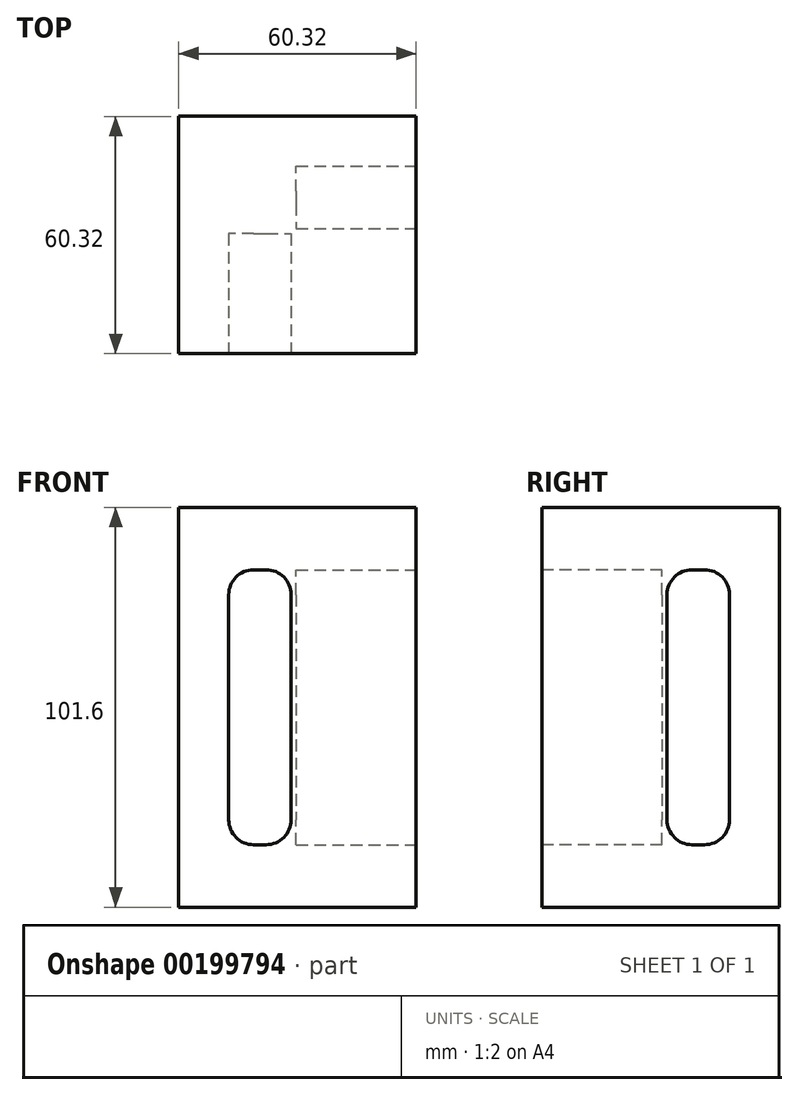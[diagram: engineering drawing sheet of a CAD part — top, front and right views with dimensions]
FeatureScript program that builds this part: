
annotation { "Feature Type Name" : "Feature", "Feature Type Description" : "" }
export const myFeature = defineFeature(function(context is Context, id is Id, definition is map)
    precondition{}
    {
        {
            var Q0;
            Q0=qCreatedBy(makeId("Top.planeOp"),FACE);
            var sketch = newSketch(context, id + "F0", { "sketchPlane" : qUnion([Q0])});
            skLineSegment(sketch, "E0.bottom", {"start": v(30.16, -30.16) * mm, "end": v(-30.16, -30.16) * mm});
            skLineSegment(sketch, "E0.top", {"start": v(30.16, 30.16) * mm, "end": v(-30.16, 30.16) * mm});
            skLineSegment(sketch, "E0.left", {"start": v(30.16, -30.16) * mm, "end": v(30.16, 30.16) * mm});
            skLineSegment(sketch, "E0.right", {"start": v(-30.16, -30.16) * mm, "end": v(-30.16, 30.16) * mm});
            skPoint(sketch, "E0.middle", {"position": v(0, 0) * mm});
            skSolve(sketch);
        }
        {
            var Q0;
            Q0 = qSketchRegion(id + "F0", true);
            extrude(context, id + "F1", {"entities" : qUnion([Q0]), "depth" : 101.6 * mm});
        }
        {
            var Q0;
            Q0=makeQuery(id+"F1.opExtrude","CAP_FACE",FACE,{"disambiguationData":[OSD([sQuery(id+"F0.wireOp",EDGE,"E0.bottom"),sQuery(id+"F0.wireOp",EDGE,"E0.top"),sQuery(id+"F0.wireOp",EDGE,"E0.left"),sQuery(id+"F0.wireOp",EDGE,"E0.right")])],"isStart":true});
            var sketch = newSketch(context, id + "F2", { "sketchPlane" : qUnion([Q0])});
            skSolve(sketch);
        }
        {
            var Q0;
            Q0=makeQuery(id+"F1.opExtrude","SWEPT_FACE",FACE,{"disambiguationData":[OSD([sQuery(id+"F0.wireOp",EDGE,"E0.bottom")])]});
            var sketch = newSketch(context, id + "F3", { "sketchPlane" : qUnion([Q0])});
            skLineSegment(sketch, "E1.bottom", {"start": v(-17.46, 85.73) * mm, "end": v(-1.59, 85.73) * mm});
            skLineSegment(sketch, "E1.top", {"start": v(-17.46, 15.88) * mm, "end": v(-1.59, 15.88) * mm});
            skLineSegment(sketch, "E1.left", {"start": v(-17.46, 85.73) * mm, "end": v(-17.46, 15.88) * mm});
            skLineSegment(sketch, "E1.right", {"start": v(-1.59, 85.73) * mm, "end": v(-1.59, 15.88) * mm});
            skSolve(sketch);
        }
        {
            var Q0;
            Q0=makeQuery(id+"F3.imprint","IMPRINT",FACE,{"disambiguationData":[TD([[makeQuery(id+"F3.imprint","IMPRINT",EDGE,{"derivedFrom":sQuery(id+"F3.wireOp",EDGE,"E1.bottom")}),-1.0]])]});
            extrude(context, id + "F4", {"entities" : qUnion([Q0]), "operationType" : NewBodyOperationType.REMOVE, "oppositeDirection" : true, "depth" : 30.48 * mm, "offsetDistance" : 25.4 * mm});
        }
        {
            var Q0;
            Q0=makeQuery(id+"F1.opExtrude","SWEPT_FACE",FACE,{"disambiguationData":[OSD([sQuery(id+"F0.wireOp",EDGE,"E0.left")])]});
            var sketch = newSketch(context, id + "F5", { "sketchPlane" : qUnion([Q0])});
            skLineSegment(sketch, "E2.bottom", {"start": v(17.46, 85.73) * mm, "end": v(1.59, 85.73) * mm});
            skLineSegment(sketch, "E2.top", {"start": v(17.46, 15.88) * mm, "end": v(1.59, 15.88) * mm});
            skLineSegment(sketch, "E2.left", {"start": v(17.46, 85.73) * mm, "end": v(17.46, 15.88) * mm});
            skLineSegment(sketch, "E2.right", {"start": v(1.59, 85.73) * mm, "end": v(1.59, 15.88) * mm});
            skSolve(sketch);
        }
        {
            var Q0;
            Q0 = qSketchRegion(id + "F5", true);
            extrude(context, id + "F6", {"entities" : qUnion([Q0]), "operationType" : NewBodyOperationType.REMOVE, "oppositeDirection" : true, "depth" : 30.48 * mm, "offsetDistance" : 25.4 * mm});
        }
        {
            var Q0;
            Q0=makeQuery(id+"F4.boolean.opBoolean","COPY",EDGE,{"derivedFrom":makeQuery(id+"F4.opExtrude","SWEPT_EDGE",EDGE,{"disambiguationData":[OSD([sQuery(id+"F3.wireOp",EDGE,"E1.bottom"),sQuery(id+"F3.wireOp",EDGE,"E1.left")])]})});
            var Q1;
            Q1=makeQuery(id+"F4.boolean.opBoolean","COPY",EDGE,{"derivedFrom":makeQuery(id+"F4.opExtrude","SWEPT_EDGE",EDGE,{"disambiguationData":[OSD([sQuery(id+"F3.wireOp",EDGE,"E1.bottom"),sQuery(id+"F3.wireOp",EDGE,"E1.right")])]})});
            var Q2;
            Q2=makeQuery(id+"F4.boolean.opBoolean","COPY",EDGE,{"derivedFrom":makeQuery(id+"F4.opExtrude","SWEPT_EDGE",EDGE,{"disambiguationData":[OSD([sQuery(id+"F3.wireOp",EDGE,"E1.top"),sQuery(id+"F3.wireOp",EDGE,"E1.left")])]})});
            var Q3;
            Q3=makeQuery(id+"F4.boolean.opBoolean","COPY",EDGE,{"derivedFrom":makeQuery(id+"F4.opExtrude","SWEPT_EDGE",EDGE,{"disambiguationData":[OSD([sQuery(id+"F3.wireOp",EDGE,"E1.top"),sQuery(id+"F3.wireOp",EDGE,"E1.right")])]})});
            var Q4;
            Q4=makeQuery(id+"F6.boolean.opBoolean","COPY",EDGE,{"derivedFrom":makeQuery(id+"F6.opExtrude","SWEPT_EDGE",EDGE,{"disambiguationData":[OSD([sQuery(id+"F5.wireOp",EDGE,"E2.bottom"),sQuery(id+"F5.wireOp",EDGE,"E2.left")])]})});
            var Q5;
            Q5=makeQuery(id+"F6.boolean.opBoolean","COPY",EDGE,{"derivedFrom":makeQuery(id+"F6.opExtrude","SWEPT_EDGE",EDGE,{"disambiguationData":[OSD([sQuery(id+"F5.wireOp",EDGE,"E2.bottom"),sQuery(id+"F5.wireOp",EDGE,"E2.right")])]})});
            var Q6;
            Q6=makeQuery(id+"F6.boolean.opBoolean","COPY",EDGE,{"derivedFrom":makeQuery(id+"F6.opExtrude","SWEPT_EDGE",EDGE,{"disambiguationData":[OSD([sQuery(id+"F5.wireOp",EDGE,"E2.top"),sQuery(id+"F5.wireOp",EDGE,"E2.right")])]})});
            var Q7;
            Q7=makeQuery(id+"F6.boolean.opBoolean","COPY",EDGE,{"derivedFrom":makeQuery(id+"F6.opExtrude","SWEPT_EDGE",EDGE,{"disambiguationData":[OSD([sQuery(id+"F5.wireOp",EDGE,"E2.top"),sQuery(id+"F5.wireOp",EDGE,"E2.left")])]})});
            fillet(context, id + "F7", {"entities" : qUnion([Q0, Q1, Q2, Q3, Q4, Q5, Q6, Q7]), "radius" : 6.35 * mm, "tangentPropagation" : true, "allowEdgeOverflow" : false});
        }
    });
